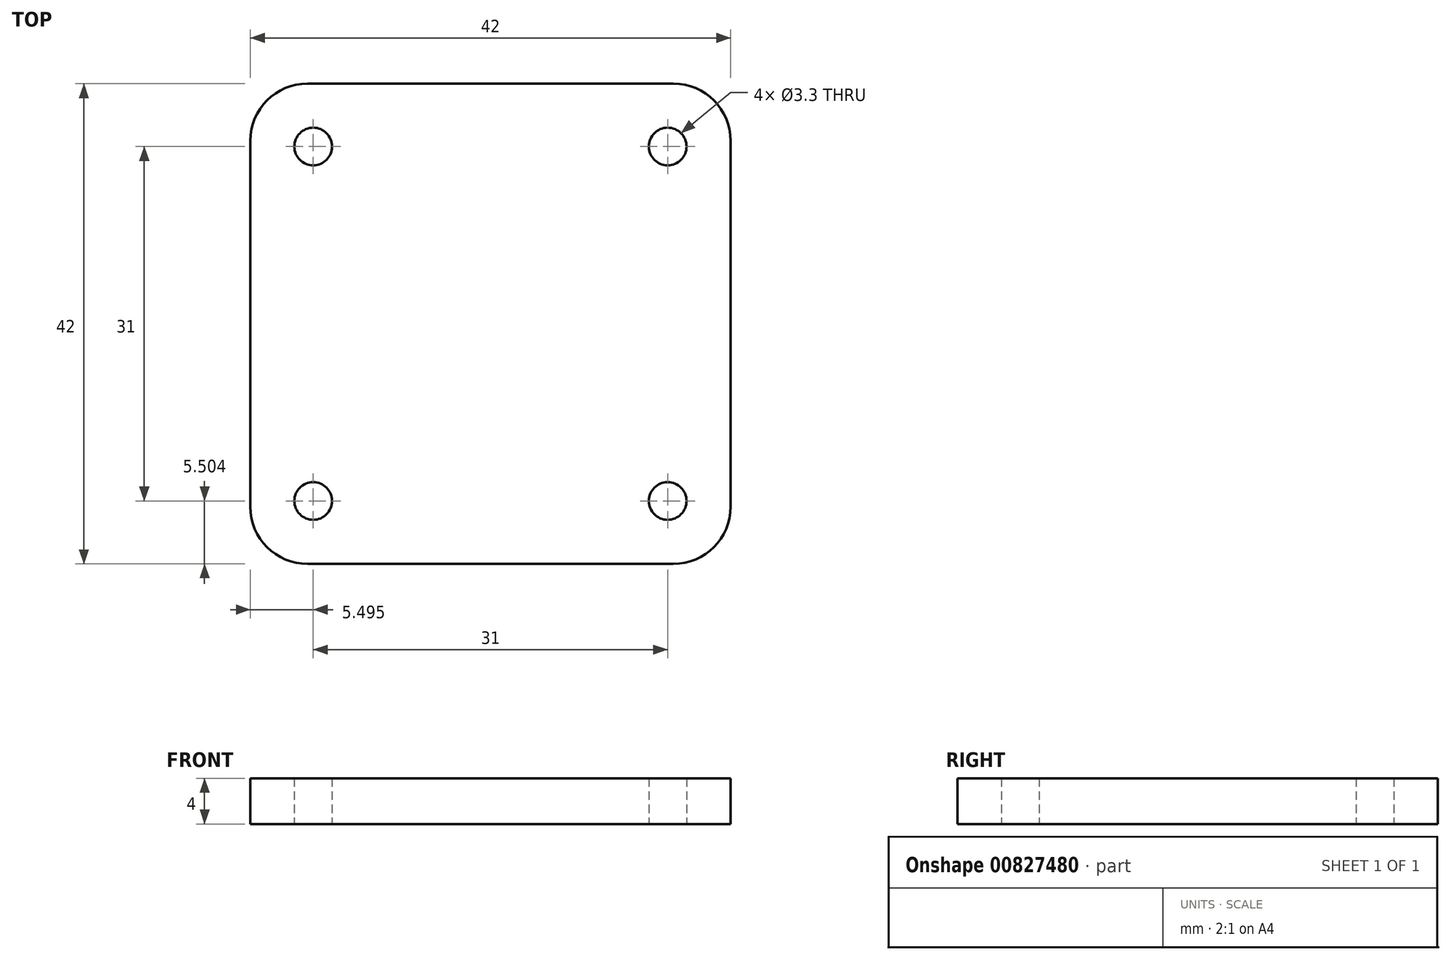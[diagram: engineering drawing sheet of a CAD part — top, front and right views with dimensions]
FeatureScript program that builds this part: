
annotation { "Feature Type Name" : "Feature", "Feature Type Description" : "" }
export const myFeature = defineFeature(function(context is Context, id is Id, definition is map)
    precondition{}
    {
        {
            var Q0;
            Q0=qCreatedBy(makeId("Top.planeOp"),FACE);
            var sketch = newSketch(context, id + "F0", { "sketchPlane" : qUnion([Q0])});
            skLineSegment(sketch, "E0.bottom", {"start": v(-8.72, 17.6) * mm, "end": v(33.28, 17.6) * mm});
            skLineSegment(sketch, "E0.top", {"start": v(-8.72, -24.4) * mm, "end": v(33.28, -24.4) * mm});
            skLineSegment(sketch, "E0.left", {"start": v(-8.72, 17.6) * mm, "end": v(-8.72, -24.4) * mm});
            skLineSegment(sketch, "E0.right", {"start": v(33.28, 17.6) * mm, "end": v(33.28, -24.4) * mm});
            skCircle(sketch, "E1", {"center": v(-3.22, 12.1) * mm, "radius": 1.65 * mm});
            skCircle(sketch, "E2", {"center": v(27.78, 12.1) * mm, "radius": 1.65 * mm});
            skCircle(sketch, "E3", {"center": v(27.78, -18.9) * mm, "radius": 1.65 * mm});
            skCircle(sketch, "E4", {"center": v(-3.22, -18.9) * mm, "radius": 1.65 * mm});
            skSolve(sketch);
        }
        {
            var Q0;
            Q0=makeQuery(id+"F0.imprint","IMPRINT",FACE,{"disambiguationData":[TD([[makeQuery(id+"F0.imprint","IMPRINT",EDGE,{"derivedFrom":sQuery(id+"F0.wireOp",EDGE,"E0.bottom")}),-1.0]])]});
            extrude(context, id + "F1", {"entities" : qUnion([Q0]), "depth" : 4 * mm, "offsetDistance" : 25 * mm});
        }
        {
            var Q0;
            Q0=makeQuery(id+"F1.opExtrude","SWEPT_EDGE",EDGE,{"disambiguationData":[OSD([sQuery(id+"F0.wireOp",EDGE,"E0.top"),sQuery(id+"F0.wireOp",EDGE,"E0.left")])]});
            var Q1;
            Q1=makeQuery(id+"F1.opExtrude","SWEPT_EDGE",EDGE,{"disambiguationData":[OSD([sQuery(id+"F0.wireOp",EDGE,"E0.top"),sQuery(id+"F0.wireOp",EDGE,"E0.right")])]});
            var Q2;
            Q2=makeQuery(id+"F1.opExtrude","SWEPT_EDGE",EDGE,{"disambiguationData":[OSD([sQuery(id+"F0.wireOp",EDGE,"E0.bottom"),sQuery(id+"F0.wireOp",EDGE,"E0.right")])]});
            var Q3;
            Q3=makeQuery(id+"F1.opExtrude","SWEPT_EDGE",EDGE,{"disambiguationData":[OSD([sQuery(id+"F0.wireOp",EDGE,"E0.bottom"),sQuery(id+"F0.wireOp",EDGE,"E0.left")])]});
            fillet(context, id + "F2", {"entities" : qUnion([Q0, Q1, Q2, Q3]), "radius" : 5 * mm, "tangentPropagation" : true, "allowEdgeOverflow" : false});
        }
    });
